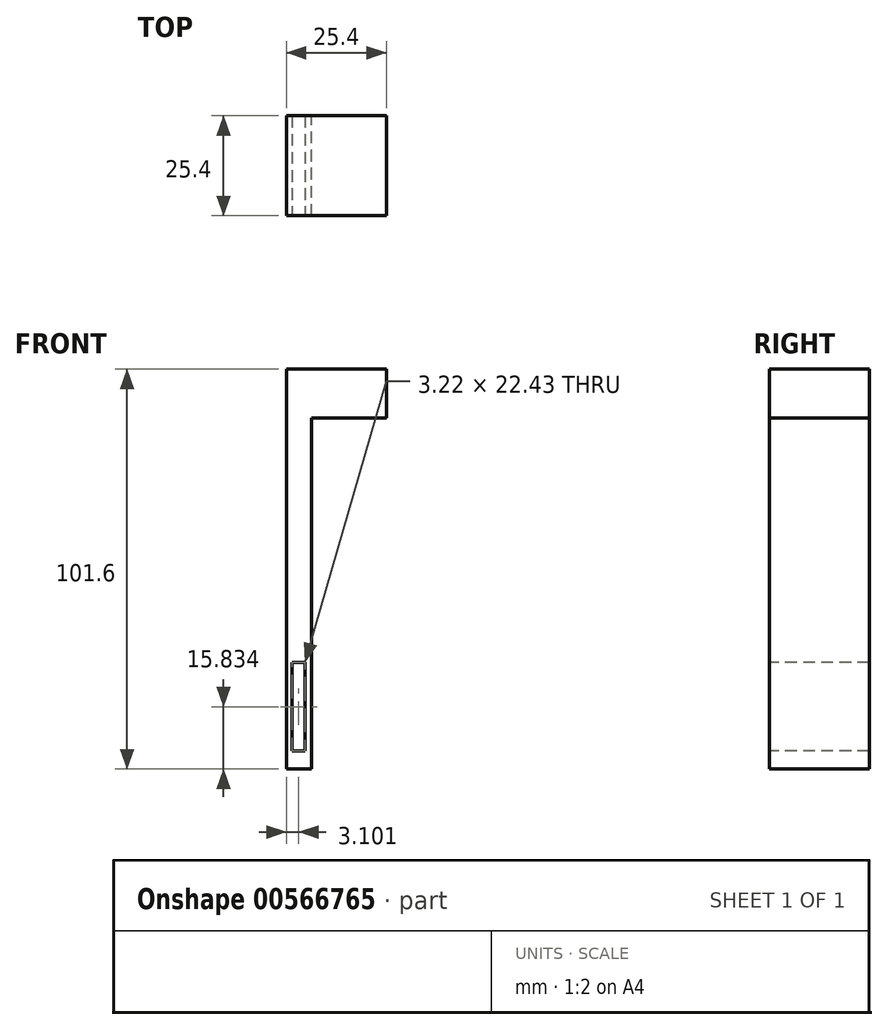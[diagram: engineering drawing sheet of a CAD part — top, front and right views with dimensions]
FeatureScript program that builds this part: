
annotation { "Feature Type Name" : "Feature", "Feature Type Description" : "" }
export const myFeature = defineFeature(function(context is Context, id is Id, definition is map)
    precondition{}
    {
        {
            var Q0;
            Q0=qCreatedBy(makeId("Front.planeOp"),FACE);
            var sketch = newSketch(context, id + "F0", { "sketchPlane" : qUnion([Q0])});
            skLineSegment(sketch, "E0.bottom", {"start": v(-29.2, 50.14) * mm, "end": v(-3.8, 50.14) * mm});
            skLineSegment(sketch, "E0.top", {"start": v(-29.2, -51.46) * mm, "end": v(-3.8, -51.46) * mm});
            skLineSegment(sketch, "E0.left", {"start": v(-29.2, 50.14) * mm, "end": v(-29.2, -51.46) * mm});
            skLineSegment(sketch, "E0.right", {"start": v(-3.8, 50.14) * mm, "end": v(-3.8, -51.46) * mm});
            skLineSegment(sketch, "E1", {"start": v(-16.5, -51.46) * mm, "end": v(-16.5, 50.14) * mm});
            skLineSegment(sketch, "E2", {"start": v(-29.2, 37.78) * mm, "end": v(-16.5, 37.78) * mm});
            skLineSegment(sketch, "E3", {"start": v(-16.5, 37.78) * mm, "end": v(-3.8, 37.78) * mm});
            skLineSegment(sketch, "E4", {"start": v(-22.85, 37.78) * mm, "end": v(-22.85, -51.46) * mm});
            skLineSegment(sketch, "E5", {"start": v(-10.15, 37.78) * mm, "end": v(-10.15, -51.46) * mm});
            skPoint(sketch, "E6.oppositeSnap0", {"position": v(-3.8, -0.66) * mm});
            skLineSegment(sketch, "E6.bottom", {"start": v(-10.15, 37.78) * mm, "end": v(-3.8, 37.78) * mm});
            skLineSegment(sketch, "E6.top", {"start": v(-10.15, 0) * mm, "end": v(-3.8, 0) * mm});
            skLineSegment(sketch, "E6.left", {"start": v(-10.15, 37.78) * mm, "end": v(-10.15, 0) * mm});
            skLineSegment(sketch, "E6.right", {"start": v(-3.8, 37.78) * mm, "end": v(-3.8, 0) * mm});
            skSolve(sketch);
        }
        {
            var Q0;
            {var subQ3=sQuery(id+"F0.wireOp",EDGE,"E4");Q0=makeQuery(id+"F0.imprint","IMPRINT",FACE,{"disambiguationData":[TD([[makeQuery(id+"F0.imprint","IMPRINT",EDGE,{"derivedFrom":subQ3}),-1.0]])]});}
            var Q1;
            {var subQ1=sQuery(id+"F0.wireOp",EDGE,"E0.left");var subQ5=sQuery(id+"F0.wireOp",EDGE,"E0.bottom");var subQ8=makeQuery(id+"F0.imprint","INTERSECT",VERTEX,{"derivedFrom":[subQ5,subQ1]});Q1=makeQuery(id+"F0.imprint","IMPRINT",FACE,{"disambiguationData":[TD([[makeQuery(id+"F0.imprint","IMPRINT",EDGE,{"disambiguationData":[TD([[subQ8,-1.0]])],"derivedFrom":subQ5}),-1.0]])]});}
            var Q2;
            {var subQ0=sQuery(id+"F0.wireOp",EDGE,"E3");Q2=makeQuery(id+"F0.imprint","IMPRINT",FACE,{"disambiguationData":[TD([[makeQuery(id+"F0.imprint","IMPRINT",EDGE,{"derivedFrom":subQ0}),1.0]])]});}
            var Q3;
            Q3=makeQuery(id+"F0.imprint","IMPRINT",FACE,{"disambiguationData":[TD([[makeQuery(id+"F0.imprint","IMPRINT",EDGE,{"derivedFrom":sQuery(id+"F0.wireOp",EDGE,"E6.bottom")}),-1.0]])]});
            extrude(context, id + "F1", {"entities" : qUnion([Q0, Q1, Q2, Q3]), "depth" : 25.4 * mm, "offsetDistance" : 25.4 * mm});
        }
        {
            var Q0;
            Q0=makeQuery(id+"F1.opExtrude","CAP_FACE",FACE,{"disambiguationData":[OSD([sQuery(id+"F0.wireOp",EDGE,"E0.bottom"),sQuery(id+"F0.wireOp",EDGE,"E0.top"),sQuery(id+"F0.wireOp",EDGE,"E0.left"),sQuery(id+"F0.wireOp",EDGE,"E0.right"),sQuery(id+"F0.wireOp",EDGE,"E2"),sQuery(id+"F0.wireOp",EDGE,"E3"),sQuery(id+"F0.wireOp",EDGE,"E4"),sQuery(id+"F0.wireOp",EDGE,"E6.top"),sQuery(id+"F0.wireOp",EDGE,"E6.left"),sQuery(id+"F0.wireOp",EDGE,"E6.right")])],"isStart":false});
            var sketch = newSketch(context, id + "F2", { "sketchPlane" : qUnion([Q0])});
            skLineSegment(sketch, "E7.bottom", {"start": v(-27.7, -24.4) * mm, "end": v(-24.5, -24.4) * mm});
            skLineSegment(sketch, "E7.top", {"start": v(-27.7, -46.84) * mm, "end": v(-24.5, -46.84) * mm});
            skLineSegment(sketch, "E7.left", {"start": v(-27.7, -24.4) * mm, "end": v(-27.7, -46.84) * mm});
            skLineSegment(sketch, "E7.right", {"start": v(-24.5, -24.4) * mm, "end": v(-24.5, -46.84) * mm});
            skSolve(sketch);
        }
        {
            var Q0;
            Q0=makeQuery(id+"F2.imprint","IMPRINT",FACE,{"disambiguationData":[TD([[makeQuery(id+"F2.imprint","IMPRINT",EDGE,{"derivedFrom":sQuery(id+"F2.wireOp",EDGE,"E7.bottom")}),-1.0]])]});
            extrude(context, id + "F3", {"entities" : qUnion([Q0]), "operationType" : NewBodyOperationType.REMOVE, "oppositeDirection" : true, "depth" : 25.4 * mm, "offsetDistance" : 25.4 * mm});
        }
    });
